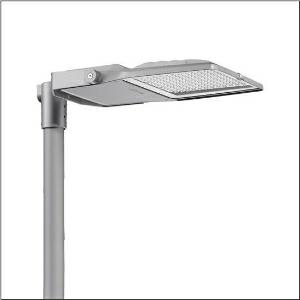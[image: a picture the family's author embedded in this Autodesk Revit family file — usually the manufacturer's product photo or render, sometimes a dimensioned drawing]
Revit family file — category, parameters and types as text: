
# Revit family: floodlight_fl_21_midi___pl61_5xa7786f4c3a_8fd3
name_source: partatom
category: Lighting Fixtures
units: mm (PartAtom-declared; Revit-internal decimal feet)

## family parameters
Cut with Voids When Loaded = No
Host = Face
Light Source = No
Part Type = Normal
Room Calculation Point = No
Round Connector Dimension = Use Diameter
Shared = No

## types (1)
- --- (1 x LED, 36640 lm, 271.6 W, 4000K)
    Apparent Load = 272 VA
    CIE Flux Codes = 33 65 98 100 100
    Color Rendering = 70
    Color Temperature = 4000K
    Default Elevation = 1800 mm
    Description = Floodlight FL 21 midi, floodlight, primary light control with lens, of PMMA, primary optical cover: protective disc, of toughened safety glass, transparent, light distribution: PL61, light emission: direct distribution, installation type: surface-mounted, LED, High Power LED, rated luminous flux: 36.640lm, luminous efficacy: 135lm/W, light colour: 740, colour temperature: 4000K, control gear: Smart Interface (Zhaga)D4i, control: overheat protection, constant luminous flux control, time-dependent luminous flux control, flexible luminous flux parameterisation, pre-setting: logarithmic dimming characteristic, with terminal, 6-pole, mains connection: 220..240V, AC, 50/60Hz, start of lifetime: 272W, end of service life: 287W, reduction: 123W, mast bracket, of diecast aluminium, powder-coated, SITECO metallic grey (DB 702S), corrosivity category C5 mid according to DIN EN ISO 12944, suitable for swimming pools, chlorine-resistant, sealing non-destructively replaceable, mast bracket, of steel, galvanised, powder-coated, SITECO metallic grey (DB 702S), Smart Interface below and above, protection rating (complete): IP66, insulation class (complete): insulation class II (safety insulation), certification: CE, ENEC, VDE, protection symbol: D, impact resistance: IK08, permissible operating ambient temperature: -40..+40°C, permissible operating ambient temperature for outdoor applications: -40..+50°C, standard: DIN EN 12944, LABS conformity tested according to VDMA 24364:2018-05, packaging unit: 1 piece

Light Distribution: PL61
    Height = 76 mm
    Lamp = 1 x LED
    Lamp Light Flux = 36640 lm
    Lamp Power = 271.6 W
    Lamp count = 1
    Length = 657 mm
    Luminous efficacy = 135 lm/W
    Manufacturer = Siteco
    ModVariant = No
    Model = 5XA7786F4C3A
    Number of Poles = 1
    OnlyDefault = Yes
    Power Factor = 1
    Product Name = Floodlight FL 21 midi | PL61
    Product group = floodlight | pylon annexe
    ProductGroupID = 6201
    Protection Class = Protection class II
    Protection Degree = IP 66
    RLX_Detail_Level = 1
    RLX_Emergency_Light_Flux = 0 lm
    RLX_Emergency_Type = 0
    RLX_Emergency_Type_DB = No
    RlxData = <blob elided: 104693 chars, md5=2de986c1>
    Socket = socket
    Standby Power = 0 W
    System Light Flux = 36640 lm
    System Power = 272 W
    Type Comments = factory setting: luminous flux: 100 % | dim-lin: 254 | 620 mA
    Type Image = l_1007123.jpg
    URL = http://relux.com
    VarID = @adj_094321
    Voltage = 0 V
    Weight = 0.00 kg
    Width = 442 mm

## geometry (parser evidence)
native form markers: Blend x4, Sweep x11
no freeform markers — native parametric forms only
